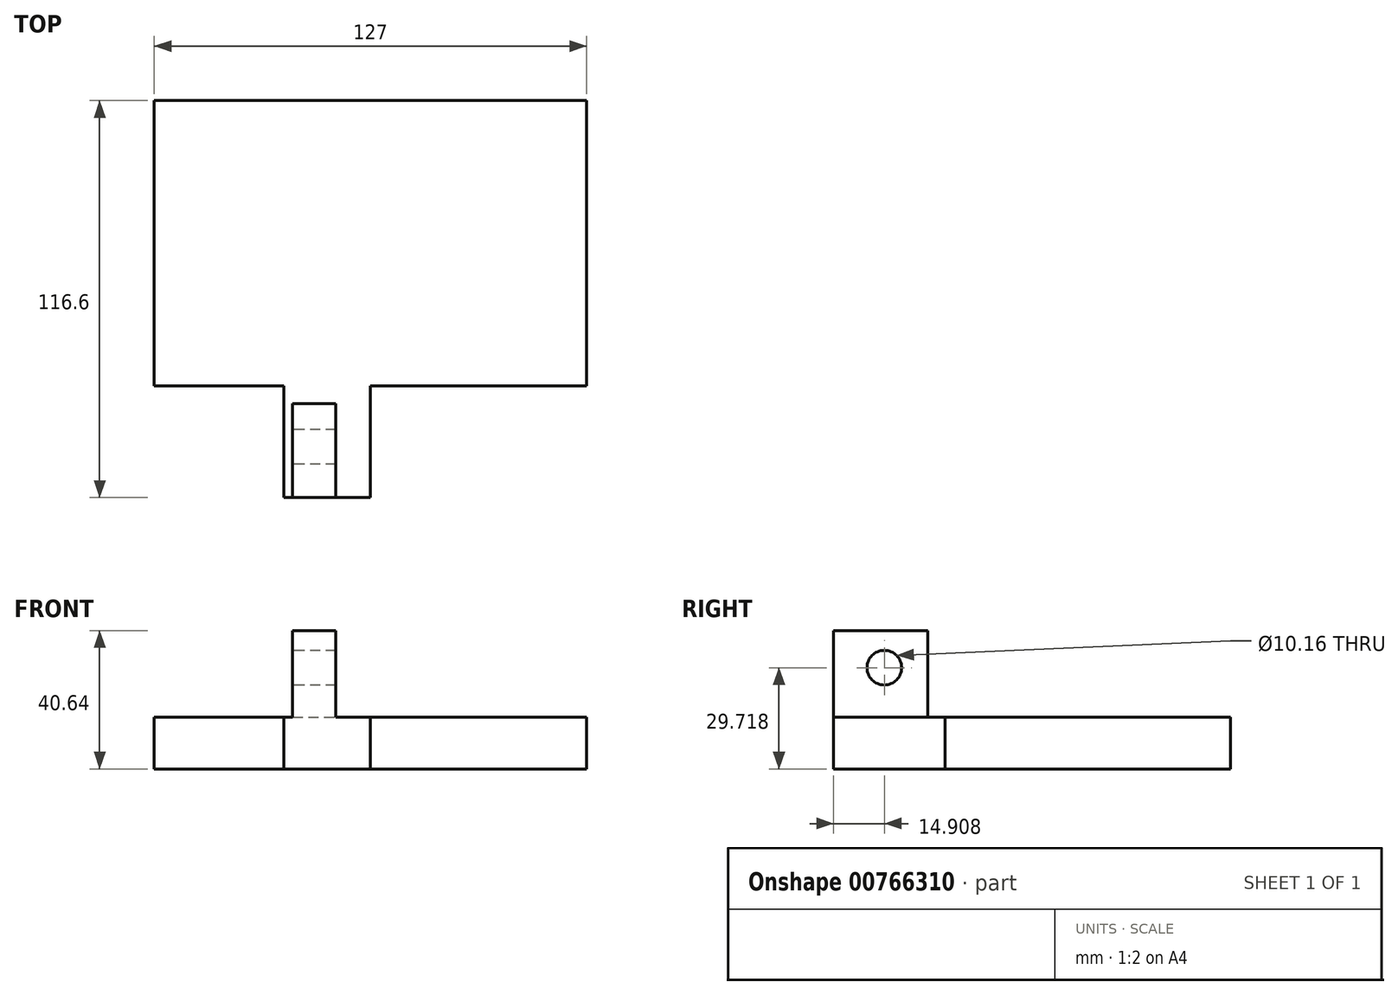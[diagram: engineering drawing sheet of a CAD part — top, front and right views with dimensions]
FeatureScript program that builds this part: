
annotation { "Feature Type Name" : "Feature", "Feature Type Description" : "" }
export const myFeature = defineFeature(function(context is Context, id is Id, definition is map)
    precondition{}
    {
        {
            var Q0;
            Q0=qCreatedBy(makeId("Top.planeOp"),FACE);
            var sketch = newSketch(context, id + "F0", { "sketchPlane" : qUnion([Q0])});
            skLineSegment(sketch, "E0.bottom", {"start": v(-298.1, 33.88) * mm, "end": v(-171.1, 33.88) * mm});
            skLineSegment(sketch, "E0.top", {"start": v(-298.1, -49.94) * mm, "end": v(-171.1, -49.94) * mm});
            skLineSegment(sketch, "E0.left", {"start": v(-298.1, 33.88) * mm, "end": v(-298.1, -49.94) * mm});
            skLineSegment(sketch, "E0.right", {"start": v(-171.1, 33.88) * mm, "end": v(-171.1, -49.94) * mm});
            skPoint(sketch, "E1.oppositeSnap0", {"position": v(-234.6, -49.94) * mm});
            skLineSegment(sketch, "E1.bottom", {"start": v(-260, -49.94) * mm, "end": v(-234.6, -49.94) * mm});
            skLineSegment(sketch, "E1.top", {"start": v(-260, -82.72) * mm, "end": v(-234.6, -82.72) * mm});
            skLineSegment(sketch, "E1.left", {"start": v(-260, -49.94) * mm, "end": v(-260, -82.72) * mm});
            skLineSegment(sketch, "E1.right", {"start": v(-234.6, -49.94) * mm, "end": v(-234.6, -82.72) * mm});
            skLineSegment(sketch, "E2.bottom", {"start": v(-257.46, -55.11) * mm, "end": v(-244.76, -55.11) * mm});
            skLineSegment(sketch, "E2.top", {"start": v(-257.46, -82.72) * mm, "end": v(-244.76, -82.72) * mm});
            skLineSegment(sketch, "E2.left", {"start": v(-257.46, -55.11) * mm, "end": v(-257.46, -82.72) * mm});
            skLineSegment(sketch, "E2.right", {"start": v(-244.76, -55.11) * mm, "end": v(-244.76, -82.72) * mm});
            skSolve(sketch);
        }
        {
            var Q0;
            Q0=makeQuery(id+"F0.imprint","IMPRINT",FACE,{"disambiguationData":[TD([[makeQuery(id+"F0.imprint","IMPRINT",EDGE,{"derivedFrom":sQuery(id+"F0.wireOp",EDGE,"E2.bottom")}),-1.0]])]});
            extrude(context, id + "F1", {"entities" : qUnion([Q0]), "depth" : 25.4 * mm, "offsetDistance" : 25.4 * mm});
        }
        {
            var Q0;
            {var subQ0=sQuery(id+"F0.wireOp",EDGE,"E1.left");var subQ11=makeQuery(id+"F0.imprint","IMPRINT",EDGE,{"derivedFrom":sQuery(id+"F0.wireOp",EDGE,"E2.bottom")});Q0=qUnion([makeQuery(id+"F0.imprint","IMPRINT",FACE,{"disambiguationData":[TD([[makeQuery(id+"F0.imprint","IMPRINT",EDGE,{"derivedFrom":sQuery(id+"F0.wireOp",EDGE,"E0.bottom")}),-1.0]])]}),makeQuery(id+"F0.imprint","IMPRINT",FACE,{"disambiguationData":[TD([[subQ11,-1.0]])]}),makeQuery(id+"F0.imprint","IMPRINT",FACE,{"disambiguationData":[TD([[makeQuery(id+"F0.imprint","IMPRINT",EDGE,{"derivedFrom":subQ0}),1.0]])]})]);}
            extrude(context, id + "F2", {"entities" : qUnion([Q0]), "operationType" : NewBodyOperationType.ADD, "oppositeDirection" : true, "depth" : 15.24 * mm, "offsetDistance" : 25.4 * mm});
        }
        {
            var Q0;
            Q0=makeQuery(id+"F1.opExtrude","SWEPT_FACE",FACE,{"disambiguationData":[OSD([sQuery(id+"F0.wireOp",EDGE,"E2.left")])]});
            var sketch = newSketch(context, id + "F3", { "sketchPlane" : qUnion([Q0])});
            skCircle(sketch, "E3", {"center": v(67.81, 14.48) * mm, "radius": 5.08 * mm});
            skSolve(sketch);
        }
        {
            var Q0;
            Q0=makeQuery(id+"F3.imprint","IMPRINT",FACE,{"disambiguationData":[TD([[makeQuery(id+"F3.imprint","IMPRINT",EDGE,{"derivedFrom":sQuery(id+"F3.wireOp",EDGE,"E3")}),1.0]])]});
            var Q1;
            Q1 = qSketchRegion(id + "F3", true);
            extrude(context, id + "F4", {"entities" : qUnion([Q0, Q1]), "operationType" : NewBodyOperationType.REMOVE, "oppositeDirection" : true, "depth" : 25.4 * mm, "offsetDistance" : 25.4 * mm});
        }
    });
